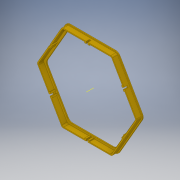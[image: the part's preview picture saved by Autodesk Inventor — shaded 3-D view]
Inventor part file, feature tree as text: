
AUTODESK INVENTOR PART (.ipt)
format: ipt  version: 2019 (Build 230136000, 136)  size: 272,384 bytes
history: native  units: mm
features: extrude x5, sketch x5, projected_geometry x3, fillet x2, other x1, pattern_circular x1
ambient origin geometry x8: Origin, YZ Plane, XZ Plane, XY Plane, X Axis, Y Axis, Z Axis, Center Point
bodies: Solid1 (feature_tree)
feature tree (17):
  extrude  "Extrusion1"  Depth=2.0mm TaperAngle=0.0deg
  extrude  "Extrusion5"  Depth=2.0mm
  extrude  "Extrusion6"  Depth=4.0mm
  fillet  "Fillet1"  Radius=7.0mm
  fillet  "Fillet2"  Radius=10.0mm
  extrude  "Extrusion7"  Depth=10.0mm
  extrude  "Extrusion8"  Depth=6.5mm TaperAngle=0.0deg
  other  "Work Axis2"
  pattern_circular  "Circular Pattern1"  [2 undecoded]
  sketch  "Sketch1"  dims[d0=175.0mm d1=2.0mm d2=0.0mm]
  sketch  "Sketch5"  dims[d15=2.0mm d16=2.0mm]
  projected_geometry  "Projected Loop4"
  sketch  "Sketch7"  dims[d17=10.0mm d18=0.0mm d19=4.0mm d20=7.0mm d21=0.0mm d22=10.0mm]
  projected_geometry  "Projected Loop6"
  sketch  "Sketch8"  dims[d23=4.0mm d24=10.0mm]
  sketch  "Sketch9"  dims[d25=3.3mm d26=6.5mm d27=0.0mm d28=4.0mm d29=3.0mm d30=5.0mm d31=0.0mm d32=60.0mm d33=360.0deg]
  projected_geometry  "Projected Loop7"
note: 2 required parameter values undecoded (feature->parameter linkage not recoverable at this tier; creation-order binding heuristic only, values carry confidence <= 0.55)
